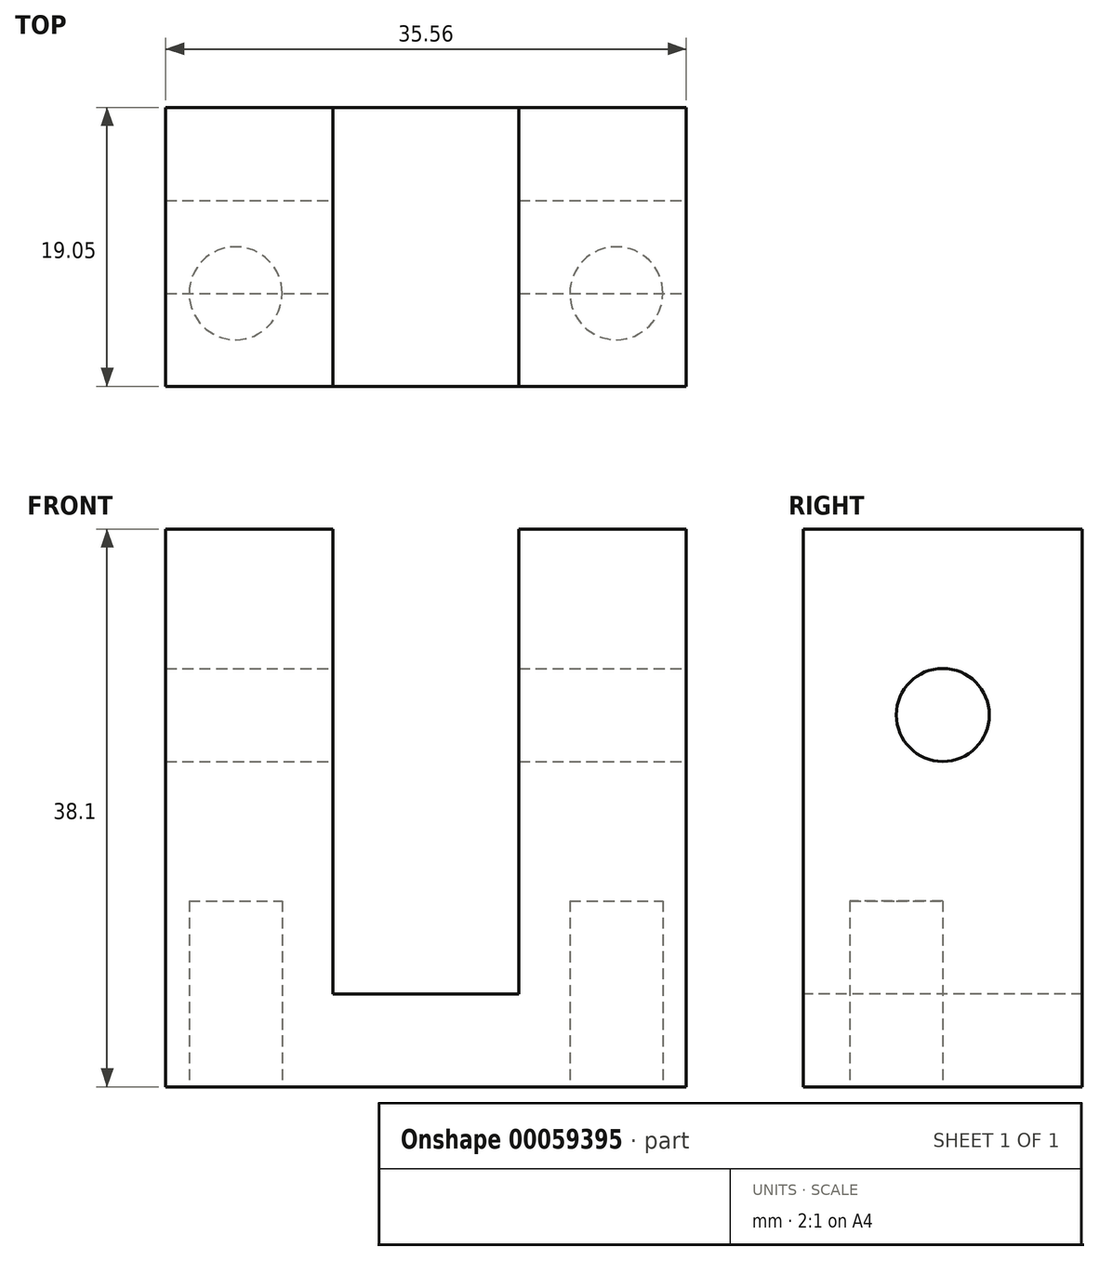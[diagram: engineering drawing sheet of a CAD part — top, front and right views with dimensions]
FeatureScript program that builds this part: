
annotation { "Feature Type Name" : "Feature", "Feature Type Description" : "" }
export const myFeature = defineFeature(function(context is Context, id is Id, definition is map)
    precondition{}
    {
        {
            var Q0;
            Q0=qCreatedBy(makeId("Front.planeOp"),FACE);
            var sketch = newSketch(context, id + "F0", { "sketchPlane" : qUnion([Q0])});
            skLineSegment(sketch, "E0", {"start": v(0, 0) * mm, "end": v(0, 38.1) * mm});
            skLineSegment(sketch, "E1", {"start": v(0, 38.1) * mm, "end": v(11.43, 38.1) * mm});
            skLineSegment(sketch, "E2", {"start": v(11.43, 38.1) * mm, "end": v(11.43, 6.35) * mm});
            skLineSegment(sketch, "E3", {"start": v(11.43, 6.35) * mm, "end": v(24.13, 6.35) * mm});
            skLineSegment(sketch, "E4", {"start": v(24.13, 6.35) * mm, "end": v(24.13, 38.1) * mm});
            skLineSegment(sketch, "E5", {"start": v(24.13, 38.1) * mm, "end": v(35.56, 38.1) * mm});
            skLineSegment(sketch, "E6", {"start": v(35.56, 38.1) * mm, "end": v(35.56, 0) * mm});
            skLineSegment(sketch, "E7", {"start": v(35.56, 0) * mm, "end": v(0, 0) * mm});
            skSolve(sketch);
        }
        {
            var Q0;
            Q0 = qSketchRegion(id + "F0", true);
            extrude(context, id + "F1", {"entities" : qUnion([Q0]), "oppositeDirection" : true, "depth" : 19.05 * mm});
        }
        {
            var Q0;
            Q0=makeQuery(id+"F1.opExtrude","SWEPT_FACE",FACE,{"disambiguationData":[OSD([sQuery(id+"F0.wireOp",EDGE,"E7")])]});
            var sketch = newSketch(context, id + "F2", { "sketchPlane" : qUnion([Q0])});
            skCircle(sketch, "E8", {"center": v(4.78, -6.35) * mm, "radius": 3.18 * mm});
            skCircle(sketch, "E9", {"center": v(30.78, -6.35) * mm, "radius": 3.18 * mm});
            skSolve(sketch);
        }
        {
            var Q0;
            Q0 = qSketchRegion(id + "F2", true);
            extrude(context, id + "F3", {"entities" : qUnion([Q0]), "operationType" : NewBodyOperationType.REMOVE, "oppositeDirection" : true, "depth" : 12.7 * mm});
        }
        {
            var Q0;
            Q0=makeQuery(id+"F1.opExtrude","SWEPT_FACE",FACE,{"disambiguationData":[OSD([sQuery(id+"F0.wireOp",EDGE,"E6")])]});
            var sketch = newSketch(context, id + "F4", { "sketchPlane" : qUnion([Q0])});
            skCircle(sketch, "E10", {"center": v(9.52, 25.4) * mm, "radius": 3.18 * mm});
            skSolve(sketch);
        }
        {
            var Q0;
            Q0 = qSketchRegion(id + "F4", true);
            extrude(context, id + "F5", {"entities" : qUnion([Q0]), "operationType" : NewBodyOperationType.REMOVE, "oppositeDirection" : true, "depth" : 76.2 * mm});
        }
    });
